# Revit family: Operable Wall - Side Stack - Unifold - Educate
name_source: partatom
category: Doors
units: mm (PartAtom-declared; Revit-internal decimal feet)

## family parameters
Always vertical = Yes
Cut with Voids When Loaded = No
OmniClass Number = 23.30.10.21.17.14
OmniClass Title = Sound Control Doors
Room Calculation Point = No
Shared = No

## types (2) — shared parameters
AluminiumExtrusions = Aluminium Annodised
Analytic Construction = <None>
Construction Type = Operable Wall
Define Thermal Properties by = Schematic Type
DoorJambDim = 75 mm
ExpanderBallonEndTotalThickness = 51 mm
ExpanderPanelDim = 201 mm  [stored 0.659449 ft]
ExpanderTravel = 150 mm
Family Revision .v.m = 0
Function = Interior
HingeFromEnds = 150 mm
Manufacturer = UNIFOLD
Model = Educate 70
Panel = Operable Wall - Panel - Unifold - Educate 70 : Educate 70 - RW42
PanelMaterial = Unifold Panel
PanelMaxWidth = 1200 mm  [stored 3.93701 ft]
StackClearanceFront = 50 mm  [stored 0.164042 ft]
StackClearanceSide = 150 mm
StandardDoorWidth = 950 mm  [stored 3.1168 ft]
Thickness = 75 mm
URL = https://unifold.com.au
zero-valued in all types: Default Elevation

## type names (no varying parameters)
- Educate 100
- Educate 70

note: [stored X ft] marks values corroborated as IEEE doubles in the binary element streams (Revit-internal decimal feet)

## geometry (parser evidence)
native form markers: Extrusion x3, Sweep x28
no freeform markers — native parametric forms only
